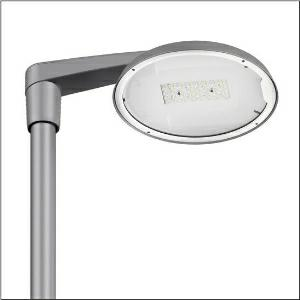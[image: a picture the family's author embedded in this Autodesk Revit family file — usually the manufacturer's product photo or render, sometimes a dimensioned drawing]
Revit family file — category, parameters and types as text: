
# Revit family: dl_r__50_iq_mini___st0_5a_5xa248b31f08ke_5f87
name_source: partatom
category: Lighting Fixtures
units: mm (PartAtom-declared; Revit-internal decimal feet)

## family parameters
Cut with Voids When Loaded = No
Host = Face
Light Source = No
Part Type = Normal
Room Calculation Point = No
Round Connector Dimension = Use Diameter
Shared = No

## types (1)
- --- (1 x LED, 5500 lm, 32.1 W, 3000K)
    Apparent Load = 32 VA
    CIE Flux Codes = 43 76 97 100 100
    Color Rendering = 70
    Color Temperature = 3000K
    Default Elevation = 1800 mm
    Description = DL® 50 iQ mini, mast luminaire, primary light control with lens, of PMMA, primary optical cover: cover, of toughened safety glass, transparent, light distribution: ST0.5a, light emission: direct distribution, primary light characteristic: asymmetric, installation type: side-entry, post-top, LED, High Power LED, rated luminous flux: 5.500lm, luminous efficacy: 171lm/W, light colour: 730, colour temperature: 3000K, control gear: iQ Street-Remote, control: optimised constant luminous flux control (CLO 2.0), Desk-Remote (wireless, voltage-free reading and setting of iQ features in the workshop via application-optimized NFC function/RFID function), Light-Fading, Smart-Wire, Night-Set, Lumen-Switch, Temp-Guard, Auto-Match, Street-Remote, mains connection: 230..240V, AC, 50/60Hz, connection cable pre-assembled, cable length: 6,5m, start of lifetime: 32W, end of service life: 33W, reduction: 16W, luminaire housing, of diecast aluminium, powder-coated, Siteco® metallic grey (DB 702S), inclination adjustable: 0°, 5°, 10° (post-top) | 0°, -5°, -10°, -15° (side-entry), please order mast post-top element or mast side-entry element separately, diameter: 500mm, height: 115mm, post-top: for spigot size d x l = 76 x 100mm; with reducer (optional accessory) 60 x 100mm | side-entry: for spigot size d x l = 60 x 100mm; with reducer (optional accessory) 42 x 100mm, mounting height: 4..6m, protection rating (complete): IP66, insulation class (complete): insulation class II (safety insulation), certification: CE, ENEC, ENEC+, VDE, impact resistance: IK08, permissible operating ambient temperature for outdoor applications: -25..+40°C, standard-compliant lighting for roads and squares, packaging unit: 1 piece

Light Distribution: ST0.5a
    Height = 115 mm
    Lamp = 1 x LED
    Lamp Light Flux = 5500 lm
    Lamp Power = 32.1 W
    Lamp count = 1
    Length = 500 mm
    Luminous efficacy = 171 lm/W
    Manufacturer = Siteco
    ModVariant = No
    Model = 5XA248B31F08KE
    Number of Poles = 1
    OnlyDefault = Yes
    Power Factor = 1
    Product Name = DL® 50 iQ mini | ST0.5a
    Product group = mast luminaire | pylon top
    ProductGroupID = 6100
    Protection Class = Protection class II
    Protection Degree = IP 66
    RLX_Detail_Level = 1
    RLX_Emergency_Light_Flux = 0 lm
    RLX_Emergency_Type = 0
    RLX_Emergency_Type_DB = No
    RlxData = <blob elided: 126845 chars, md5=f30b277d>
    Socket = socket
    Standby Power = 0 W
    System Light Flux = 5500 lm
    System Power = 32 W
    Type Comments = factory setting: luminous flux: 100 % | dim-lin: 254 | 343 mA
    Type Image = l_1251794.jpg
    URL = http://relux.com
    VarID = @adj_164475
    Voltage = 0 V
    Weight = 0.00 kg
    Width = 0 mm  [stored 0 ft]

note: [stored X ft] marks values corroborated as IEEE doubles in the binary element streams (Revit-internal decimal feet)

## geometry (parser evidence)
native form markers: Blend x4, Sweep x11
no freeform markers — native parametric forms only
